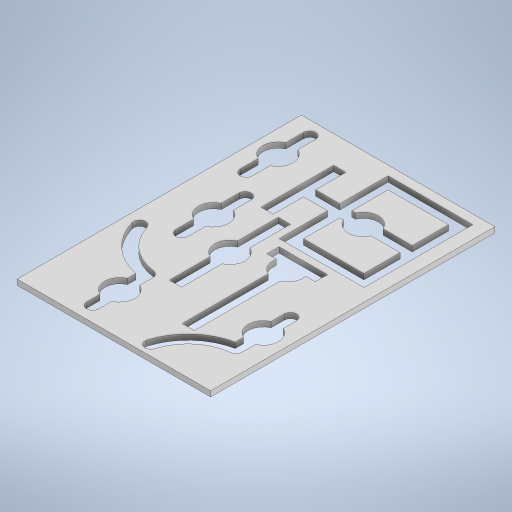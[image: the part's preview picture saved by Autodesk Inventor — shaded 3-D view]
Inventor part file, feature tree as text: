
AUTODESK INVENTOR PART (.ipt)
format: ipt  version: 2023 (Build 270158000, 158)  size: 349,184 bytes
history: native  units: mm
features: other x11, reference x8, extrude x1, sketch x1
ambient origin geometry x8: Origin, YZ Plane, XZ Plane, XY Plane, X Axis, Y Axis, Z Axis, Center Point
bodies: Body1 (feature_tree)
feature tree (21):
  other  "Sólido1"
  extrude  "Extrusión1"  [1 undecoded]
  sketch  "Boceto1"  dims[d0=9.0mm d1=0.0mm]
  reference  "Referencia1"
  reference  "Referencia2"
  reference  "Referencia3"
  reference  "Referencia4"
  reference  "Referencia5"
  reference  "Referencia6"
  reference  "Referencia7"
  reference  "Referencia8"
  other  "<userpath>\OneDrive\Robotica\Proyecto-Rob\Piezas\TablaPortaCositas.iam"
  other  "TablaPortaCositas.iam"
  other  "BaseParaTodo:1"
  other  "EslabonTransmisor:1"
  other  "EslabonTransmisor:2"
  other  "BaseGripper:1"
  other  "T:2"
  other  "PlacaRetencion:1"
  other  "Pinzas:3"
  other  "Pinzas:5"
note: 1 required parameter value undecoded (feature->parameter linkage not recoverable at this tier; creation-order binding heuristic only, values carry confidence <= 0.55)
